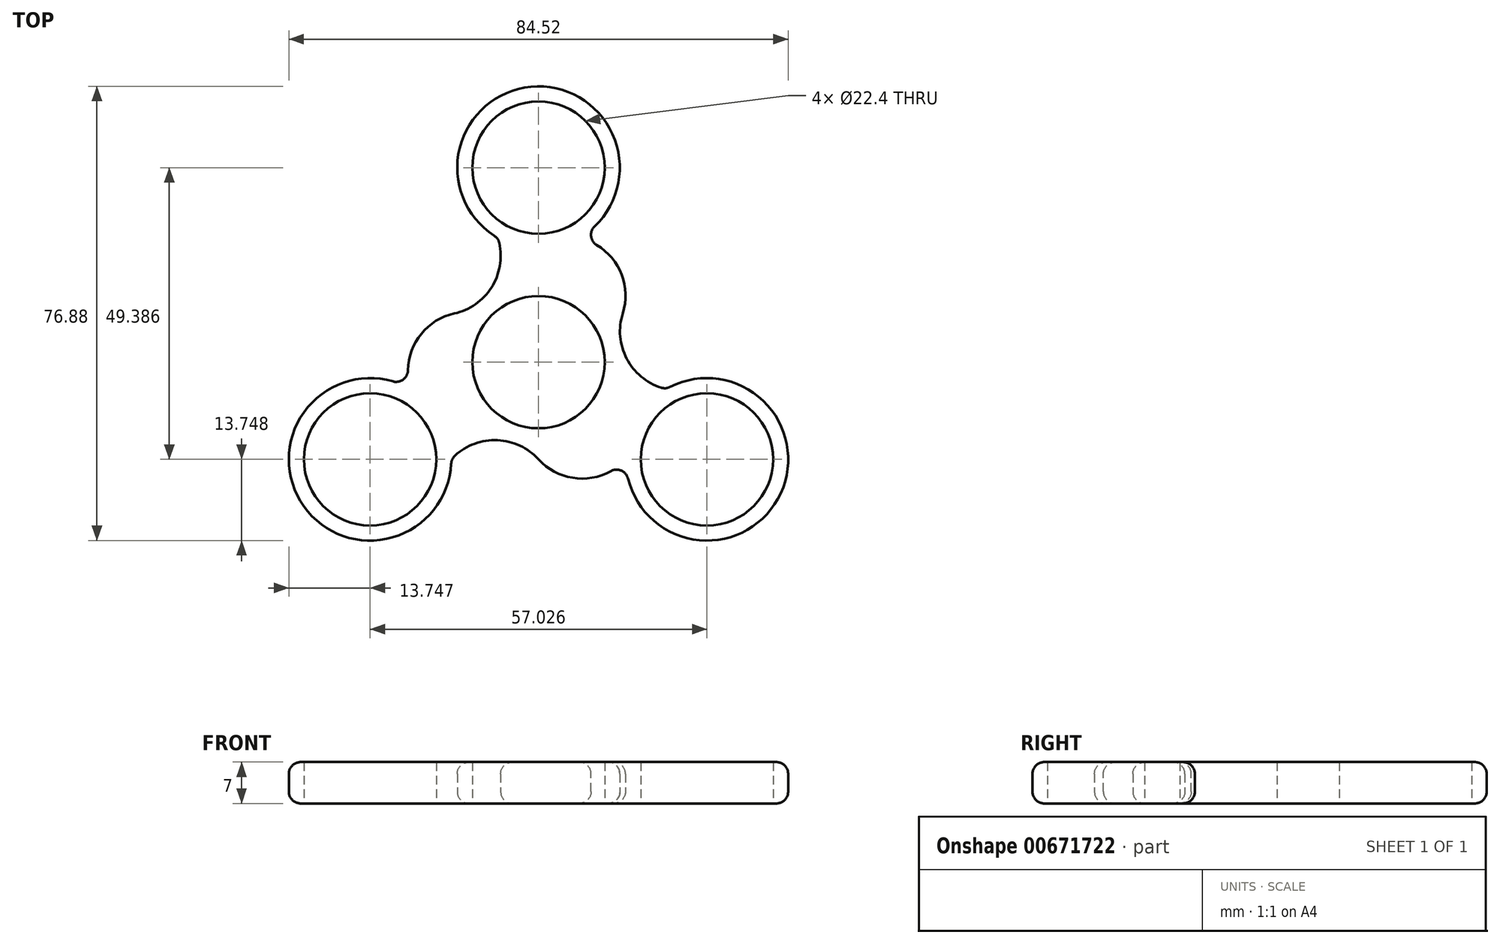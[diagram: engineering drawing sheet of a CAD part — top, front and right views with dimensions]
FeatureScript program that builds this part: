
annotation { "Feature Type Name" : "Feature", "Feature Type Description" : "" }
export const myFeature = defineFeature(function(context is Context, id is Id, definition is map)
    precondition{}
    {
        {
            var Q0;
            Q0=qCreatedBy(makeId("Top.planeOp"),FACE);
            var sketch = newSketch(context, id + "F0", { "sketchPlane" : qUnion([Q0])});
            skCircle(sketch, "E0", {"center": v(0, 0) * mm, "radius": 11.2 * mm});
            skCircle(sketch, "E1", {"center": v(0, 32.92) * mm, "radius": 11.2 * mm});
            skArc(sketch, "E2", {"start": v(6.87, 21.02) * mm, "mid": v(0, 46.67) * mm, "end": v(-6.87, 21.02) * mm});
            skArc(sketch, "E3.1.1", {"start": v(-21.64, -4.55) * mm, "mid": v(-40.42, -23.34) * mm, "end": v(-14.76, -16.46) * mm});
            skCircle(sketch, "E3.1.3", {"center": v(-28.51, -16.46) * mm, "radius": 11.2 * mm});
            skArc(sketch, "E3.2.1", {"start": v(14.76, -16.46) * mm, "mid": v(40.42, -23.34) * mm, "end": v(21.64, -4.55) * mm});
            skCircle(sketch, "E3.2.3", {"center": v(28.51, -16.46) * mm, "radius": 11.2 * mm});
            skLineSegment(sketch, "E4", {"start": v(-18.81, -10.86) * mm, "end": v(-16.6, -9.59) * mm, "construction": true});
            skLineSegment(sketch, "E5", {"start": v(0, 32.92) * mm, "end": v(6.87, 21.02) * mm, "construction": true});
            skPoint(sketch, "E6.start.orphan", {"position": v(14.26, 8.23) * mm});
            skLineSegment(sketch, "E7.trimOffspring", {"start": v(-11.9, -6.88) * mm, "end": v(-9.7, -5.6) * mm, "construction": true});
            skLineSegment(sketch, "E8.trimOffspring", {"start": v(21.64, -4.55) * mm, "end": v(22.91, -6.76) * mm, "construction": true});
            skLineSegment(sketch, "E9", {"start": v(-28.51, -16.46) * mm, "end": v(0, 0) * mm, "construction": true});
            skLineSegment(sketch, "E10", {"start": v(0, 0) * mm, "end": v(40.16, 23.19) * mm, "construction": true});
            skArc(sketch, "E11", {"start": v(14.26, 8.23) * mm, "mid": v(15.13, 0.21) * mm, "end": v(21.64, -4.55) * mm});
            skArc(sketch, "E12", {"start": v(14.26, 8.23) * mm, "mid": v(13.38, 16.25) * mm, "end": v(6.87, 21.02) * mm});
            skArc(sketch, "E13.1.0", {"start": v(-14.26, 8.23) * mm, "mid": v(-20.76, 3.47) * mm, "end": v(-21.64, -4.55) * mm});
            skArc(sketch, "E13.1.1", {"start": v(-14.26, 8.23) * mm, "mid": v(-7.75, 13) * mm, "end": v(-6.87, 21.02) * mm});
            skArc(sketch, "E13.2.0", {"start": v(0, -16.46) * mm, "mid": v(7.38, -19.72) * mm, "end": v(14.76, -16.46) * mm});
            skArc(sketch, "E13.2.1", {"start": v(0, -16.46) * mm, "mid": v(-7.38, -13.2) * mm, "end": v(-14.76, -16.46) * mm});
            skSolve(sketch);
        }
        {
            var Q0;
            Q0 = qSketchRegion(id + "F0", true);
            extrude(context, id + "F1", {"entities" : qUnion([Q0]), "depth" : 7 * mm, "offsetDistance" : 25 * mm});
        }
        {
            var Q0;
            Q0=makeQuery(id+"F1.opExtrude","SWEPT_EDGE",EDGE,{"disambiguationData":[OSD([sQuery(id+"F0.wireOp",EDGE,"E3.1.1"),sQuery(id+"F0.wireOp",EDGE,"E13.2.1")])]});
            var Q1;
            Q1=makeQuery(id+"F1.opExtrude","SWEPT_EDGE",EDGE,{"disambiguationData":[OSD([sQuery(id+"F0.wireOp",EDGE,"E3.2.1"),sQuery(id+"F0.wireOp",EDGE,"E13.2.0")])]});
            var Q2;
            Q2=makeQuery(id+"F1.opExtrude","SWEPT_EDGE",EDGE,{"disambiguationData":[OSD([sQuery(id+"F0.wireOp",EDGE,"E2"),sQuery(id+"F0.wireOp",EDGE,"E13.1.1")])]});
            var Q3;
            Q3=makeQuery(id+"F1.opExtrude","SWEPT_EDGE",EDGE,{"disambiguationData":[OSD([sQuery(id+"F0.wireOp",EDGE,"E3.1.1"),sQuery(id+"F0.wireOp",EDGE,"E13.1.0")])]});
            var Q4;
            Q4=makeQuery(id+"F1.opExtrude","SWEPT_EDGE",EDGE,{"disambiguationData":[OSD([sQuery(id+"F0.wireOp",EDGE,"E2"),sQuery(id+"F0.wireOp",EDGE,"E12")])]});
            var Q5;
            Q5=makeQuery(id+"F1.opExtrude","SWEPT_EDGE",EDGE,{"disambiguationData":[OSD([sQuery(id+"F0.wireOp",EDGE,"E3.2.1"),sQuery(id+"F0.wireOp",EDGE,"E11")])]});
            fillet(context, id + "F2", {"entities" : qUnion([Q0, Q1, Q2, Q3, Q4, Q5]), "radius" : 2 * mm, "tangentPropagation" : true, "allowEdgeOverflow" : false});
        }
        {
            var Q0;
            Q0=makeQuery(id+"F1.opExtrude","CAP_EDGE",EDGE,{"disambiguationData":[OSD([sQuery(id+"F0.wireOp",EDGE,"E13.1.1")])],"isStart":true});
            var Q1;
            Q1=makeQuery(id+"F1.opExtrude","CAP_EDGE",EDGE,{"disambiguationData":[OSD([sQuery(id+"F0.wireOp",EDGE,"E13.2.0")])],"isStart":false});
            fillet(context, id + "F3", {"entities" : qUnion([Q0, Q1]), "radius" : 2 * mm, "tangentPropagation" : true, "allowEdgeOverflow" : false});
        }
    });
